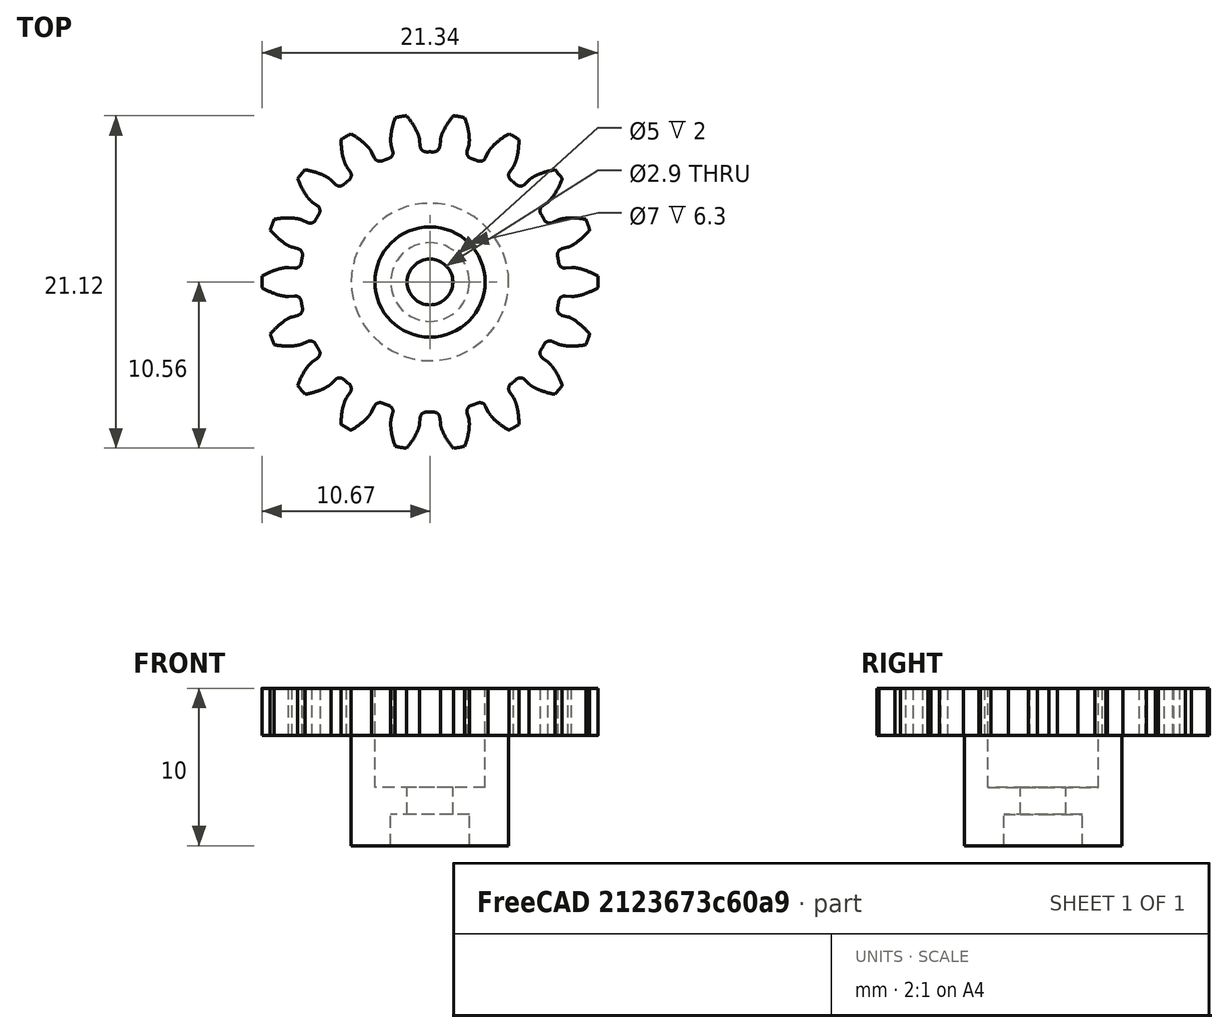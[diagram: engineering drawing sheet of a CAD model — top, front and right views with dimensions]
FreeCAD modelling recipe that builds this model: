
FCSTD DOCUMENT  (FreeCAD 0.17R13541 (Git))
Label: gear 18 high (new)
License: All rights reserved
LicenseURL: http://en.wikipedia.org/wiki/All_rights_reserved
objects: Part::Cylinder×6, Part::Cut×5, Part::Part2DObjectPython×1, Part::Extrusion×1, Part::MultiFuse×1
note: 14 computed .brp shape members not serialized (recipe doc carries the construction recipe); baked Part::Feature solids carry a one-line shape summary decoded from their .brp

FEATURE [Part::Part2DObjectPython] InvoluteGear  label="Engranaje 1 raw"  # Draft 2D object (typed FeaturePython)
  ExternalGear = true
  HighPrecision = true
  Modules = 1.0667
  NumberOfTeeth = 18
  PressureAngle = 20
  expr: Modules = 1.0667
FEATURE [Part::Extrusion] Extrude  label="Engranaje 1"
  Base = -> InvoluteGear
  Dir = (0,0,1)
  DirMode = 2
  FaceMakerClass = Part::FaceMakerBullseye
  LengthFwd = 3
  LengthRev = 0
  Solid = true
  Symmetric = false
FEATURE [Part::Cylinder] Cylinder  label="Cilindro"
  Angle = 360
  AttacherType = Attacher::AttachEngine3D
  Height = 10
  Placement = pos=(0,0,-2) rot=(0,0,1;0rad)
  Radius = 1.45
FEATURE [Part::Cut] Cut  label="Engranaje 1 agujereado"
  Base = -> Extrude
  Refine = true
  Tool = -> Cylinder
FEATURE [Part::Cylinder] Cylinder001  label="Cilindro exterior"
  Angle = 360
  AttacherType = Attacher::AttachEngine3D
  Height = 7
  Placement = pos=(0,0,-7) rot=(0,0,1;0rad)
  Radius = 5
FEATURE [Part::Cylinder] Cylinder002  label="Cilindro interior"
  Angle = 360
  AttacherType = Attacher::AttachEngine3D
  Height = 2
  Placement = pos=(0,0,-7) rot=(0,0,1;0rad)
  Radius = 2.5
FEATURE [Part::Cut] Cut001  label="Cilindro inferior"
  Base = -> Cylinder001
  Refine = true
  Tool = -> Cylinder002
FEATURE [Part::Cylinder] Cylinder003  label="Cilindro superior"
  Angle = 360
  AttacherType = Attacher::AttachEngine3D
  Height = 6.3
  Placement = pos=(0,0,-3.3) rot=(0,0,1;0rad)
  Radius = 3.5
FEATURE [Part::Cut] Cut002
  Base = -> Cut
  Refine = true
  Tool = -> Cylinder003
FEATURE [Part::MultiFuse] Fusion  label="Engranaje 2 previo"
  Refine = true
  Shapes = -> [Cut001,Cut002]
FEATURE [Part::Cylinder] Cylinder004  label="Cilindro adicional"
  Angle = 360
  AttacherType = Attacher::AttachEngine3D
  Height = 20
  Placement = pos=(0,0,-10) rot=(0,0,1;0rad)
  Radius = 1.45
FEATURE [Part::Cut] Cut003  label="Engranaje 2 previo 2"
  Base = -> Fusion
  Refine = true
  Tool = -> Cylinder004
FEATURE [Part::Cylinder] Cylinder005  label="Cilindro adicional 2"
  Angle = 360
  AttacherType = Attacher::AttachEngine3D
  Height = 6.3
  Placement = pos=(0,0,-3.3) rot=(0,0,1;0rad)
  Radius = 3.5
FEATURE [Part::Cut] Cut004  label="Engranaje 2 final"
  Base = -> Cut003
  Refine = true
  Tool = -> Cylinder005
